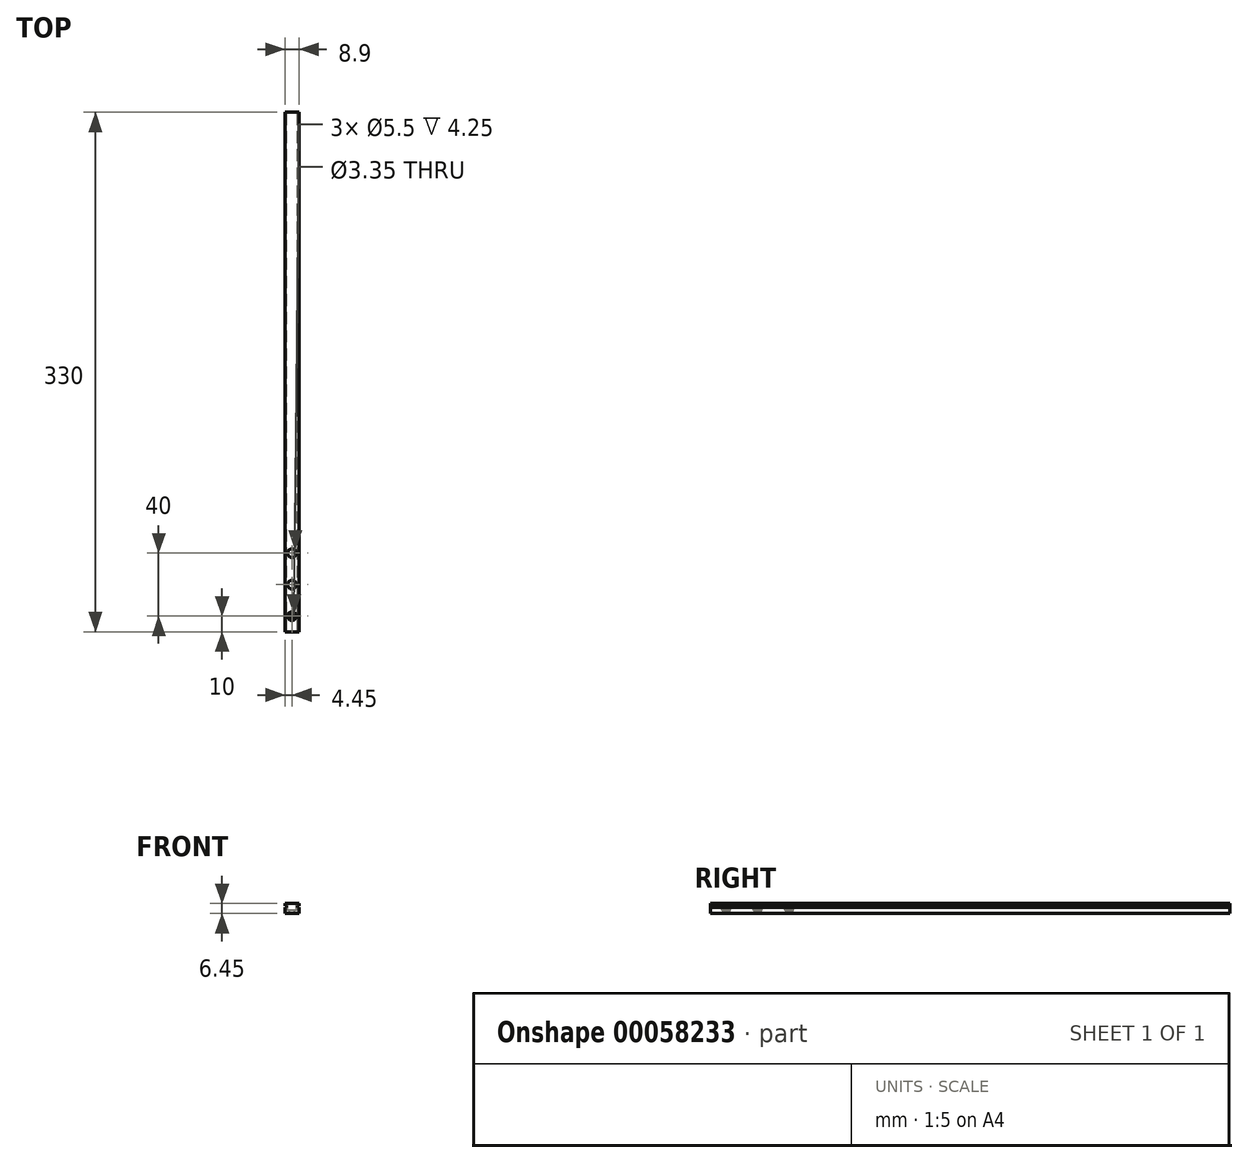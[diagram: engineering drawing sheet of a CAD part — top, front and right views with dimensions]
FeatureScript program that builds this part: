
annotation { "Feature Type Name" : "Feature", "Feature Type Description" : "" }
export const myFeature = defineFeature(function(context is Context, id is Id, definition is map)
    precondition{}
    {
        {
            var Q0;
            Q0=qCreatedBy(makeId("Front.planeOp"),FACE);
            var sketch = newSketch(context, id + "F0", { "sketchPlane" : qUnion([Q0])});
            skLineSegment(sketch, "E0", {"start": v(-4.45, 0) * mm, "end": v(-4.45, 4) * mm});
            skLineSegment(sketch, "E1", {"start": v(-4.45, 4) * mm, "end": v(-3.45, 4) * mm});
            skLineSegment(sketch, "E2", {"start": v(-3.45, 4) * mm, "end": v(-3.45, 4.95) * mm});
            skLineSegment(sketch, "E3", {"start": v(-3.45, 4.95) * mm, "end": v(-4.45, 4.95) * mm});
            skLineSegment(sketch, "E4", {"start": v(-4.45, 4.95) * mm, "end": v(-4.45, 6.45) * mm});
            skLineSegment(sketch, "E5", {"start": v(0, 0) * mm, "end": v(0, 8.72) * mm, "construction": true});
            skLineSegment(sketch, "E6.MirrorCS", {"start": v(4.45, 0) * mm, "end": v(4.45, 4) * mm});
            skLineSegment(sketch, "E7.MirrorCS", {"start": v(4.45, 4) * mm, "end": v(3.45, 4) * mm});
            skLineSegment(sketch, "E8.MirrorCS", {"start": v(3.45, 4.95) * mm, "end": v(4.45, 4.95) * mm});
            skLineSegment(sketch, "E9.MirrorCS", {"start": v(4.45, 4.95) * mm, "end": v(4.45, 6.45) * mm});
            skLineSegment(sketch, "E10.MirrorCS", {"start": v(3.45, 4) * mm, "end": v(3.45, 4.95) * mm});
            skLineSegment(sketch, "E11", {"start": v(-4.45, 0) * mm, "end": v(4.45, 0) * mm});
            skLineSegment(sketch, "E12", {"start": v(-4.45, 6.45) * mm, "end": v(4.45, 6.45) * mm});
            skSolve(sketch);
        }
        {
            var Q0;
            Q0=qSketchRegion(id+"F0",true);
            extrude(context, id + "F1", {"entities" : qUnion([Q0]), "depth" : 330 * mm});
        }
        {
            var Q0;
            Q0=makeQuery(id+"F1.opExtrude","SWEPT_FACE",FACE,{"disambiguationData":[OSD([sQuery(id+"F0.wireOp",EDGE,"E12")])]});
            var sketch = newSketch(context, id + "F2", { "sketchPlane" : qUnion([Q0])});
            skLineSegment(sketch, "E13", {"start": v(0, -330) * mm, "end": v(0, 0) * mm, "construction": true});
            skCircle(sketch, "E14", {"center": v(0, -320) * mm, "radius": 2.75 * mm});
            skCircle(sketch, "E15.0.1.0", {"center": v(0, -300) * mm, "radius": 2.75 * mm});
            skCircle(sketch, "E15.0.2.0", {"center": v(0, -280) * mm, "radius": 2.75 * mm});
            skLineSegment(sketch, "E15.direction1", {"start": v(0, -320) * mm, "end": v(19.44, -320) * mm, "construction": true});
            skLineSegment(sketch, "E15.direction2", {"start": v(0, -320) * mm, "end": v(0, -300) * mm, "construction": true});
            skSolve(sketch);
        }
        {
            var Q0;
            Q0=qSketchRegion(id+"F2",true);
            extrude(context, id + "F3", {"entities" : qUnion([Q0]), "operationType" : NewBodyOperationType.REMOVE, "oppositeDirection" : true, "depth" : 4.25 * mm});
        }
        {
            var Q0;
            Q0=makeQuery(id+"F3.boolean.opBoolean","COPY",FACE,{"derivedFrom":makeQuery(id+"F3.opExtrude","CAP_FACE",FACE,{"disambiguationData":[OSD([sQuery(id+"F2.wireOp",EDGE,"E14")])],"isStart":false})});
            var sketch = newSketch(context, id + "F4", { "sketchPlane" : qUnion([Q0])});
            skCircle(sketch, "E16", {"center": v(0, -320) * mm, "radius": 1.68 * mm});
            skSolve(sketch);
        }
        {
            var Q0;
            Q0=qSketchRegion(id+"F4",true);
            extrude(context, id + "F5", {"entities" : qUnion([Q0]), "operationType" : NewBodyOperationType.REMOVE, "endBound" : BoundingType.THROUGH_ALL, "oppositeDirection" : true, "depth" : 25 * mm});
        }
    });
